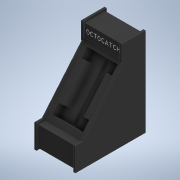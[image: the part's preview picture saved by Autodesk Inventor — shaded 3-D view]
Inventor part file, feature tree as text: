
AUTODESK INVENTOR PART (.ipt)
format: ipt  version: 2020 (Build 240168000, 168)  size: 428,032 bytes
history: native  units: mm
features: extrude x5, sketch x4, plane x1, mirror x1
ambient origin geometry x8: Origin, YZ Plane, XZ Plane, XY Plane, X Axis, Y Axis, Z Axis, Center Point
bodies: Solid1 (feature_tree)
feature tree (11):
  extrude  "Extrusion1"  Depth=1000.0mm
  extrude  "Extrusion3"  Depth=300.0mm
  extrude  "Extrusion4"  Depth=250.0mm
  extrude  "Extrusion5"  Depth=30.0mm
  extrude  "Extrusion6"  Depth=30.0mm
  plane  "Work Plane1"
  mirror  "Mirror1"
  sketch  "Sketch3"  dims[d0=1000.0mm d1=6.981317mm]
  sketch  "Sketch4"  dims[d2=100.0mm d3=300.0mm]
  sketch  "Sketch5"  dims[d4=550.0mm d5=0.0mm d8=250.0mm]
  sketch  "Sketch6"  dims[d9=300.0mm d10=520.0mm d11=80.0mm d12=460.0mm d13=40.0mm d14=80.0mm d15=460.0mm d16=40.0mm d17=130.0mm d18=0.0mm d21=110.0mm d22=100.0mm d23=60.0mm d24=60.0mm d25=0.0mm d30=200.0mm d31=300.0mm d32=3.0mm d33=0.0mm d35=30.0mm d36=0.0mm]
